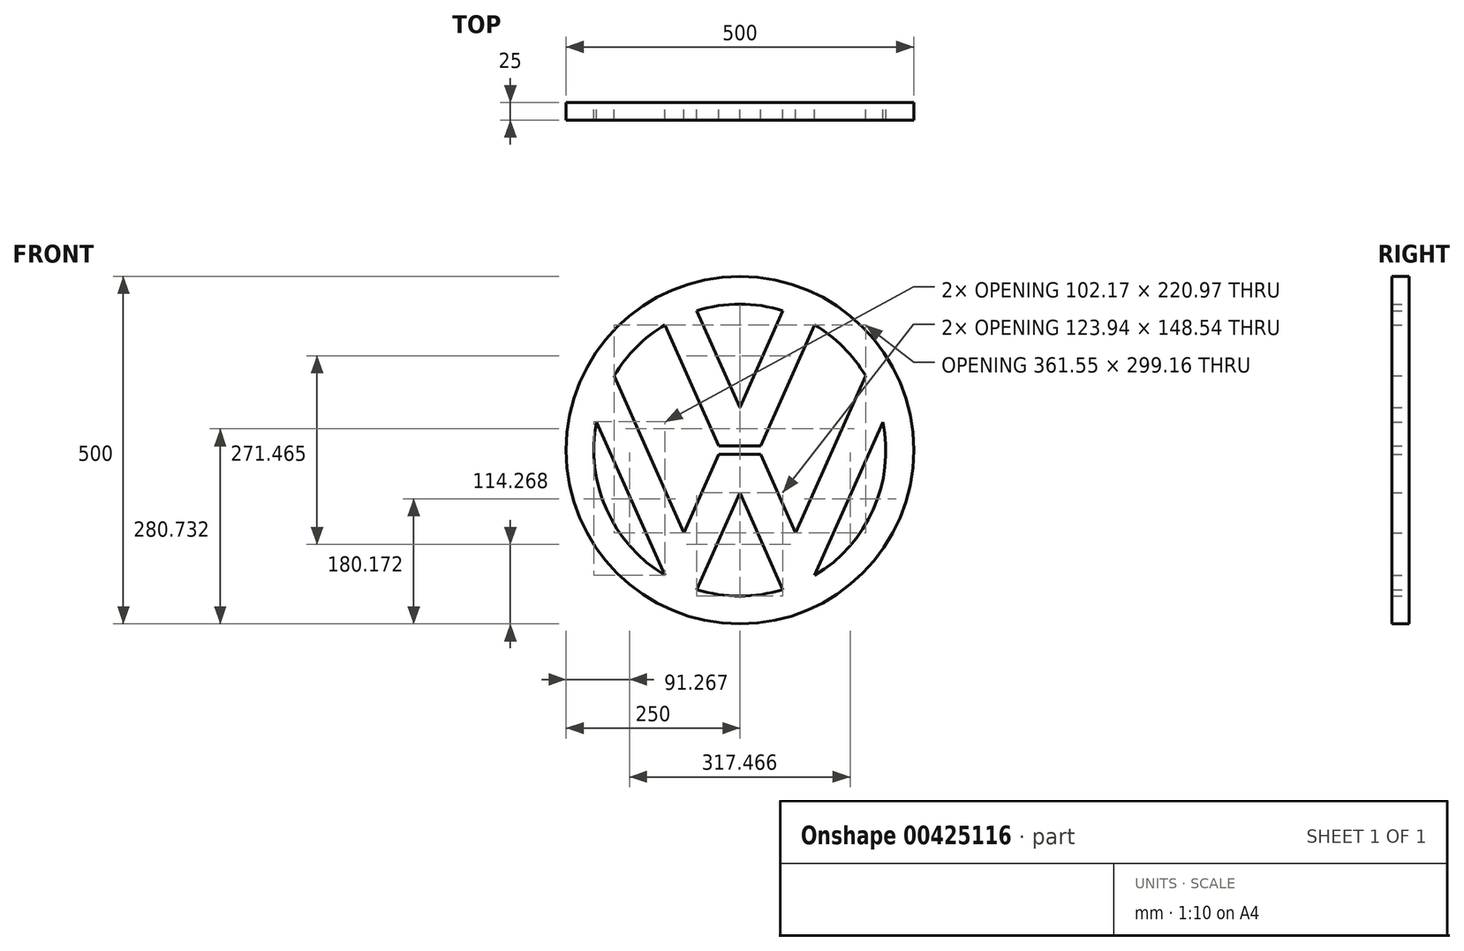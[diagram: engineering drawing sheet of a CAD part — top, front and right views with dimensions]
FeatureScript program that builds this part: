
annotation { "Feature Type Name" : "Feature", "Feature Type Description" : "" }
export const myFeature = defineFeature(function(context is Context, id is Id, definition is map)
    precondition{}
    {
        {
            var Q0;
            Q0=qCreatedBy(makeId("Front.planeOp"),FACE);
            var sketch = newSketch(context, id + "F0", { "sketchPlane" : qUnion([Q0])});
            skCircle(sketch, "E0", {"center": v(0, 0) * mm, "radius": 250 * mm});
            skLineSegment(sketch, "E1", {"start": v(0, 266.87) * mm, "end": v(0, -267.6) * mm, "construction": true});
            skLineSegment(sketch, "E2", {"start": v(0, 0) * mm, "end": v(101.68, 228.39) * mm});
            skLineSegment(sketch, "E3", {"start": v(-250, 0) * mm, "end": v(250, 0) * mm, "construction": true});
            skLineSegment(sketch, "E4.MirrorCS", {"start": v(0, 0) * mm, "end": v(101.68, -228.39) * mm});
            skLineSegment(sketch, "E5.MirrorCS", {"start": v(0, 0) * mm, "end": v(-101.68, 228.39) * mm});
            skLineSegment(sketch, "E6.MirrorCS", {"start": v(0, 0) * mm, "end": v(-101.68, -228.39) * mm});
            skCircle(sketch, "E7", {"center": v(0, 0) * mm, "radius": 210 * mm});
            skLineSegment(sketch, "E8.0", {"start": v(-27.37, 0) * mm, "end": v(-124.52, 218.22) * mm});
            skLineSegment(sketch, "E8.1", {"start": v(-27.37, 0) * mm, "end": v(-124.52, -218.22) * mm});
            skLineSegment(sketch, "E9.0", {"start": v(27.37, 0) * mm, "end": v(124.52, 218.22) * mm});
            skLineSegment(sketch, "E9.1", {"start": v(27.37, 0) * mm, "end": v(124.52, -218.22) * mm});
            skLineSegment(sketch, "E10.0", {"start": v(0, 61.46) * mm, "end": v(78.85, 238.55) * mm});
            skLineSegment(sketch, "E10.1", {"start": v(0, 61.46) * mm, "end": v(-78.85, 238.55) * mm});
            skLineSegment(sketch, "E11.0", {"start": v(0, -61.46) * mm, "end": v(78.85, -238.55) * mm});
            skLineSegment(sketch, "E11.1", {"start": v(0, -61.46) * mm, "end": v(-78.85, -238.55) * mm});
            skLineSegment(sketch, "E12", {"start": v(107.65, -180.31) * mm, "end": v(206.03, 40.66) * mm});
            skLineSegment(sketch, "E13", {"start": v(-107.65, -180.31) * mm, "end": v(-206.03, 40.66) * mm});
            skLineSegment(sketch, "E14.0", {"start": v(-80.28, -118.85) * mm, "end": v(-180.77, 106.87) * mm});
            skLineSegment(sketch, "E15.0", {"start": v(80.28, -118.85) * mm, "end": v(180.77, 106.87) * mm});
            skLineSegment(sketch, "E16", {"start": v(-30.15, 6.25) * mm, "end": v(30.15, 6.25) * mm});
            skLineSegment(sketch, "E17.MirrorCS", {"start": v(-30.15, -6.25) * mm, "end": v(30.15, -6.25) * mm});
            skSolve(sketch);
        }
        {
            var Q0;
            {var subQ6=sQuery(id+"F0.wireOp",EDGE,"E8.0");var subQ8=sQuery(id+"F0.wireOp",EDGE,"E0");var subQ9=makeQuery(id+"F0.imprint","INTERSECT",VERTEX,{"derivedFrom":[subQ8,subQ6]});Q0=makeQuery(id+"F0.imprint","IMPRINT",FACE,{"disambiguationData":[TD([[makeQuery(id+"F0.imprint","IMPRINT",EDGE,{"disambiguationData":[TD([[subQ9,-1.0]])],"derivedFrom":subQ8}),1.0]])]});}
            var Q1;
            {var subQ0=sQuery(id+"F0.wireOp",EDGE,"E5.MirrorCS");var subQ1=sQuery(id+"F0.wireOp",EDGE,"E0");var subQ2=makeQuery(id+"F0.imprint","INTERSECT",VERTEX,{"derivedFrom":[subQ1,subQ0]});Q1=makeQuery(id+"F0.imprint","IMPRINT",FACE,{"disambiguationData":[TD([[makeQuery(id+"F0.imprint","IMPRINT",EDGE,{"disambiguationData":[TD([[subQ2,-1.0]])],"derivedFrom":subQ1}),1.0]])]});}
            var Q2;
            {var subQ0=sQuery(id+"F0.wireOp",EDGE,"E5.MirrorCS");var subQ1=sQuery(id+"F0.wireOp",EDGE,"E0");var subQ2=makeQuery(id+"F0.imprint","INTERSECT",VERTEX,{"derivedFrom":[subQ1,subQ0]});Q2=makeQuery(id+"F0.imprint","IMPRINT",FACE,{"disambiguationData":[TD([[makeQuery(id+"F0.imprint","IMPRINT",EDGE,{"disambiguationData":[TD([[subQ2,1.0]])],"derivedFrom":subQ1}),1.0]])]});}
            var Q3;
            {var subQ0=sQuery(id+"F0.wireOp",EDGE,"E10.0");var subQ1=sQuery(id+"F0.wireOp",EDGE,"E0");var subQ2=makeQuery(id+"F0.imprint","INTERSECT",VERTEX,{"derivedFrom":[subQ1,subQ0]});Q3=makeQuery(id+"F0.imprint","IMPRINT",FACE,{"disambiguationData":[TD([[makeQuery(id+"F0.imprint","IMPRINT",EDGE,{"disambiguationData":[TD([[subQ2,-1.0]])],"derivedFrom":subQ1}),1.0]])]});}
            var Q4;
            {var subQ0=sQuery(id+"F0.wireOp",EDGE,"E2");var subQ1=sQuery(id+"F0.wireOp",EDGE,"E0");var subQ2=makeQuery(id+"F0.imprint","INTERSECT",VERTEX,{"derivedFrom":[subQ1,subQ0]});Q4=makeQuery(id+"F0.imprint","IMPRINT",FACE,{"disambiguationData":[TD([[makeQuery(id+"F0.imprint","IMPRINT",EDGE,{"disambiguationData":[TD([[subQ2,-1.0]])],"derivedFrom":subQ1}),1.0]])]});}
            var Q5;
            {var subQ2=sQuery(id+"F0.wireOp",EDGE,"E9.0");var subQ8=sQuery(id+"F0.wireOp",EDGE,"E0");var subQ9=makeQuery(id+"F0.imprint","INTERSECT",VERTEX,{"derivedFrom":[subQ8,subQ2]});Q5=makeQuery(id+"F0.imprint","IMPRINT",FACE,{"disambiguationData":[TD([[makeQuery(id+"F0.imprint","IMPRINT",EDGE,{"disambiguationData":[TD([[subQ9,1.0]])],"derivedFrom":subQ8}),1.0]])]});}
            var Q6;
            {var subQ0=sQuery(id+"F0.wireOp",EDGE,"E2");var subQ1=sQuery(id+"F0.wireOp",EDGE,"E0");var subQ2=makeQuery(id+"F0.imprint","INTERSECT",VERTEX,{"derivedFrom":[subQ1,subQ0]});Q6=makeQuery(id+"F0.imprint","IMPRINT",FACE,{"disambiguationData":[TD([[makeQuery(id+"F0.imprint","IMPRINT",EDGE,{"disambiguationData":[TD([[subQ2,1.0]])],"derivedFrom":subQ1}),1.0]])]});}
            var Q7;
            {var subQ0=sQuery(id+"F0.wireOp",EDGE,"E12");Q7=makeQuery(id+"F0.imprint","IMPRINT",FACE,{"disambiguationData":[TD([[makeQuery(id+"F0.imprint","IMPRINT",EDGE,{"derivedFrom":subQ0}),1.0]])]});}
            var Q8;
            {var subQ0=sQuery(id+"F0.wireOp",EDGE,"E4.MirrorCS");var subQ1=sQuery(id+"F0.wireOp",EDGE,"E0");var subQ2=makeQuery(id+"F0.imprint","INTERSECT",VERTEX,{"derivedFrom":[subQ1,subQ0]});Q8=makeQuery(id+"F0.imprint","IMPRINT",FACE,{"disambiguationData":[TD([[makeQuery(id+"F0.imprint","IMPRINT",EDGE,{"disambiguationData":[TD([[subQ2,-1.0]])],"derivedFrom":subQ1}),1.0]])]});}
            var Q9;
            {var subQ0=sQuery(id+"F0.wireOp",EDGE,"E4.MirrorCS");var subQ1=sQuery(id+"F0.wireOp",EDGE,"E0");var subQ2=makeQuery(id+"F0.imprint","INTERSECT",VERTEX,{"derivedFrom":[subQ1,subQ0]});Q9=makeQuery(id+"F0.imprint","IMPRINT",FACE,{"disambiguationData":[TD([[makeQuery(id+"F0.imprint","IMPRINT",EDGE,{"disambiguationData":[TD([[subQ2,1.0]])],"derivedFrom":subQ1}),1.0]])]});}
            var Q10;
            {var subQ5=sQuery(id+"F0.wireOp",EDGE,"E4.MirrorCS");var subQ9=sQuery(id+"F0.wireOp",EDGE,"E17.MirrorCS");var subQ10=makeQuery(id+"F0.imprint","INTERSECT",VERTEX,{"derivedFrom":[subQ5,subQ9]});Q10=makeQuery(id+"F0.imprint","IMPRINT",FACE,{"disambiguationData":[TD([[makeQuery(id+"F0.imprint","IMPRINT",EDGE,{"disambiguationData":[TD([[subQ10,-1.0]])],"derivedFrom":subQ5}),-1.0]])]});}
            var Q11;
            {var subQ4=sQuery(id+"F0.wireOp",EDGE,"E4.MirrorCS");var subQ6=sQuery(id+"F0.wireOp",EDGE,"E17.MirrorCS");var subQ7=makeQuery(id+"F0.imprint","INTERSECT",VERTEX,{"derivedFrom":[subQ4,subQ6]});Q11=makeQuery(id+"F0.imprint","IMPRINT",FACE,{"disambiguationData":[TD([[makeQuery(id+"F0.imprint","IMPRINT",EDGE,{"disambiguationData":[TD([[subQ7,-1.0]])],"derivedFrom":subQ4}),1.0]])]});}
            var Q12;
            {var subQ0=sQuery(id+"F0.wireOp",EDGE,"E11.1");var subQ1=sQuery(id+"F0.wireOp",EDGE,"E0");var subQ2=makeQuery(id+"F0.imprint","INTERSECT",VERTEX,{"derivedFrom":[subQ1,subQ0]});Q12=makeQuery(id+"F0.imprint","IMPRINT",FACE,{"disambiguationData":[TD([[makeQuery(id+"F0.imprint","IMPRINT",EDGE,{"disambiguationData":[TD([[subQ2,-1.0]])],"derivedFrom":subQ1}),1.0]])]});}
            var Q13;
            {var subQ0=sQuery(id+"F0.wireOp",EDGE,"E6.MirrorCS");var subQ1=sQuery(id+"F0.wireOp",EDGE,"E0");var subQ2=makeQuery(id+"F0.imprint","INTERSECT",VERTEX,{"derivedFrom":[subQ1,subQ0]});Q13=makeQuery(id+"F0.imprint","IMPRINT",FACE,{"disambiguationData":[TD([[makeQuery(id+"F0.imprint","IMPRINT",EDGE,{"disambiguationData":[TD([[subQ2,-1.0]])],"derivedFrom":subQ1}),1.0]])]});}
            var Q14;
            {var subQ0=sQuery(id+"F0.wireOp",EDGE,"E6.MirrorCS");var subQ1=sQuery(id+"F0.wireOp",EDGE,"E0");var subQ2=makeQuery(id+"F0.imprint","INTERSECT",VERTEX,{"derivedFrom":[subQ1,subQ0]});Q14=makeQuery(id+"F0.imprint","IMPRINT",FACE,{"disambiguationData":[TD([[makeQuery(id+"F0.imprint","IMPRINT",EDGE,{"disambiguationData":[TD([[subQ2,1.0]])],"derivedFrom":subQ1}),1.0]])]});}
            var Q15;
            {var subQ4=sQuery(id+"F0.wireOp",EDGE,"E6.MirrorCS");var subQ6=sQuery(id+"F0.wireOp",EDGE,"E17.MirrorCS");var subQ8=makeQuery(id+"F0.imprint","INTERSECT",VERTEX,{"derivedFrom":[subQ4,subQ6]});Q15=makeQuery(id+"F0.imprint","IMPRINT",FACE,{"disambiguationData":[TD([[makeQuery(id+"F0.imprint","IMPRINT",EDGE,{"disambiguationData":[TD([[subQ8,-1.0]])],"derivedFrom":subQ4}),-1.0]])]});}
            var Q16;
            {var subQ0=sQuery(id+"F0.wireOp",EDGE,"E13");Q16=makeQuery(id+"F0.imprint","IMPRINT",FACE,{"disambiguationData":[TD([[makeQuery(id+"F0.imprint","IMPRINT",EDGE,{"derivedFrom":subQ0}),-1.0]])]});}
            var Q17;
            {var subQ0=sQuery(id+"F0.wireOp",EDGE,"E16");var subQ1=sQuery(id+"F0.wireOp",EDGE,"E5.MirrorCS");var subQ2=makeQuery(id+"F0.imprint","INTERSECT",VERTEX,{"derivedFrom":[subQ1,subQ0]});Q17=makeQuery(id+"F0.imprint","IMPRINT",FACE,{"disambiguationData":[TD([[makeQuery(id+"F0.imprint","IMPRINT",EDGE,{"disambiguationData":[TD([[subQ2,-1.0]])],"derivedFrom":subQ1}),1.0]])]});}
            var Q18;
            {var subQ0=sQuery(id+"F0.wireOp",EDGE,"E16");var subQ1=sQuery(id+"F0.wireOp",EDGE,"E2");var subQ2=makeQuery(id+"F0.imprint","INTERSECT",VERTEX,{"derivedFrom":[subQ1,subQ0]});Q18=makeQuery(id+"F0.imprint","IMPRINT",FACE,{"disambiguationData":[TD([[makeQuery(id+"F0.imprint","IMPRINT",EDGE,{"disambiguationData":[TD([[subQ2,-1.0]])],"derivedFrom":subQ1}),-1.0]])]});}
            var Q19;
            {var subQ1=sQuery(id+"F0.wireOp",EDGE,"E2");var subQ9=sQuery(id+"F0.wireOp",EDGE,"E16");var subQ11=makeQuery(id+"F0.imprint","INTERSECT",VERTEX,{"derivedFrom":[subQ1,subQ9]});Q19=makeQuery(id+"F0.imprint","IMPRINT",FACE,{"disambiguationData":[TD([[makeQuery(id+"F0.imprint","IMPRINT",EDGE,{"disambiguationData":[TD([[subQ11,-1.0]])],"derivedFrom":subQ1}),1.0]])]});}
            extrude(context, id + "F1", {"entities" : qUnion([Q0, Q1, Q2, Q3, Q4, Q5, Q6, Q7, Q8, Q9, Q10, Q11, Q12, Q13, Q14, Q15, Q16, Q17, Q18, Q19]), "depth" : 25 * mm});
        }
    });
